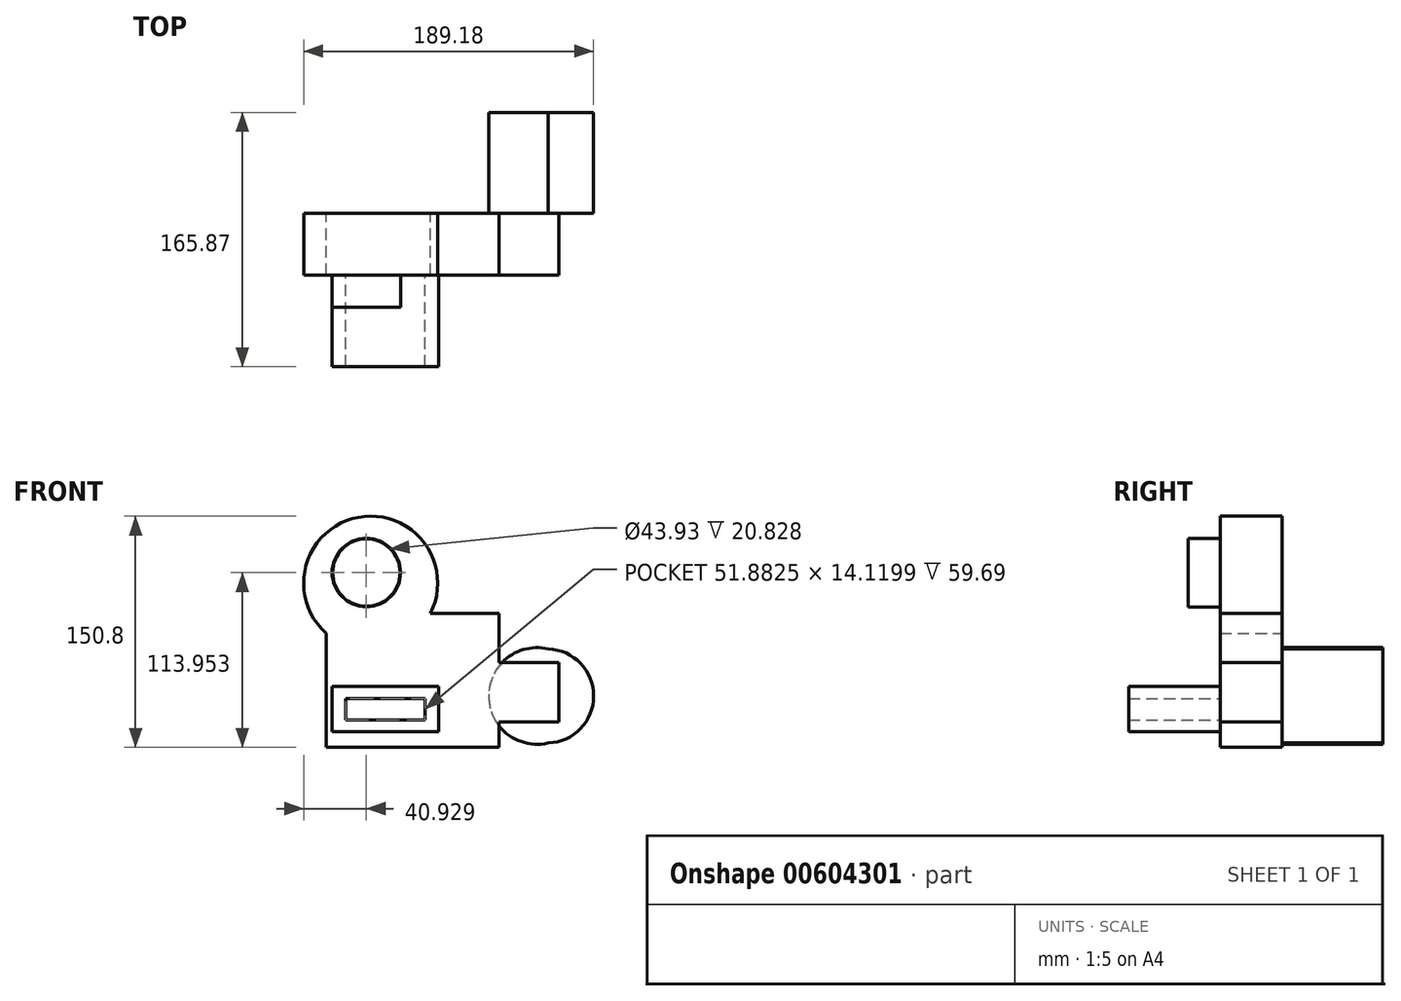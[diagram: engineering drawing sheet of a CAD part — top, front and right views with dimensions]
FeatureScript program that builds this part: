
annotation { "Feature Type Name" : "Feature", "Feature Type Description" : "" }
export const myFeature = defineFeature(function(context is Context, id is Id, definition is map)
    precondition{}
    {
        {
            var Q0;
            Q0=qCreatedBy(makeId("Front.planeOp"),FACE);
            var sketch = newSketch(context, id + "F0", { "sketchPlane" : qUnion([Q0])});
            skCircle(sketch, "E0", {"center": v(-44.26, 41.78) * mm, "radius": 43.7 * mm});
            skLineSegment(sketch, "E1.bottom", {"start": v(-67.47, -9.9) * mm, "end": v(78.62, -9.9) * mm});
            skLineSegment(sketch, "E1.top", {"start": v(-67.47, -48.6) * mm, "end": v(78.62, -48.6) * mm});
            skLineSegment(sketch, "E1.left", {"start": v(-67.47, -9.9) * mm, "end": v(-67.47, -48.6) * mm});
            skLineSegment(sketch, "E1.right", {"start": v(78.62, -9.9) * mm, "end": v(78.62, -48.6) * mm});
            skLineSegment(sketch, "E2.bottom", {"start": v(39.62, 21.98) * mm, "end": v(-73.36, 21.98) * mm});
            skLineSegment(sketch, "E2.top", {"start": v(39.62, -65.3) * mm, "end": v(-73.36, -65.3) * mm});
            skLineSegment(sketch, "E2.left", {"start": v(39.62, 21.98) * mm, "end": v(39.62, -65.3) * mm});
            skLineSegment(sketch, "E2.right", {"start": v(-73.36, 21.98) * mm, "end": v(-73.36, -65.3) * mm});
            skSolve(sketch);
        }
        {
            var Q0;
            Q0 = qSketchRegion(id + "F0", true);
            extrude(context, id + "F1", {"entities" : qUnion([Q0]), "depth" : 40.4 * mm, "offsetDistance" : 25.4 * mm});
        }
        {
            var Q0;
            Q0=qCreatedBy(makeId("Front.planeOp"),FACE);
            var sketch = newSketch(context, id + "F2", { "sketchPlane" : qUnion([Q0])});
            skCircle(sketch, "E3", {"center": v(-47.03, 48.64) * mm, "radius": 22.33 * mm});
            skCircle(sketch, "E4", {"center": v(-47.03, 48.64) * mm, "radius": 21.96 * mm});
            skSolve(sketch);
        }
        {
            var Q0;
            Q0 = qSketchRegion(id + "F2", true);
            extrude(context, id + "F3", {"entities" : qUnion([Q0]), "operationType" : NewBodyOperationType.ADD, "depth" : 61.2 * mm, "offsetDistance" : 25.4 * mm});
        }
        {
            var Q0;
            Q0=qCreatedBy(makeId("Front.planeOp"),FACE);
            var sketch = newSketch(context, id + "F4", { "sketchPlane" : qUnion([Q0])});
            skLineSegment(sketch, "E5.bottom", {"start": v(0, -25.57) * mm, "end": v(-69.36, -25.57) * mm});
            skLineSegment(sketch, "E5.top", {"start": v(0, -55.12) * mm, "end": v(-69.36, -55.12) * mm});
            skLineSegment(sketch, "E5.left", {"start": v(0, -25.57) * mm, "end": v(0, -55.12) * mm});
            skLineSegment(sketch, "E5.right", {"start": v(-69.36, -25.57) * mm, "end": v(-69.36, -55.12) * mm});
            skLineSegment(sketch, "E6.bottom", {"start": v(-8.61, -33.45) * mm, "end": v(-60.5, -33.45) * mm});
            skLineSegment(sketch, "E6.top", {"start": v(-8.61, -47.57) * mm, "end": v(-60.5, -47.57) * mm});
            skLineSegment(sketch, "E6.left", {"start": v(-8.61, -33.45) * mm, "end": v(-8.61, -47.57) * mm});
            skLineSegment(sketch, "E6.right", {"start": v(-60.5, -33.45) * mm, "end": v(-60.5, -47.57) * mm});
            skSolve(sketch);
        }
        {
            var Q0;
            Q0 = qSketchRegion(id + "F4", true);
            extrude(context, id + "F5", {"entities" : qUnion([Q0]), "operationType" : NewBodyOperationType.ADD, "depth" : 100.08 * mm, "offsetDistance" : 25.4 * mm});
        }
        {
            var Q0;
            Q0=qCreatedBy(makeId("Front.planeOp"),FACE);
            var sketch = newSketch(context, id + "F6", { "sketchPlane" : qUnion([Q0])});
            skCircle(sketch, "E7", {"center": v(64.29, -31.8) * mm, "radius": 31.53 * mm});
            skCircle(sketch, "E8", {"center": v(70.53, -31.8) * mm, "radius": 30.7 * mm});
            skSolve(sketch);
        }
        {
            var Q0;
            Q0 = qSketchRegion(id + "F6", true);
            extrude(context, id + "F7", {"entities" : qUnion([Q0]), "operationType" : NewBodyOperationType.ADD, "oppositeDirection" : true, "depth" : 65.8 * mm, "offsetDistance" : 25.4 * mm});
        }
    });
